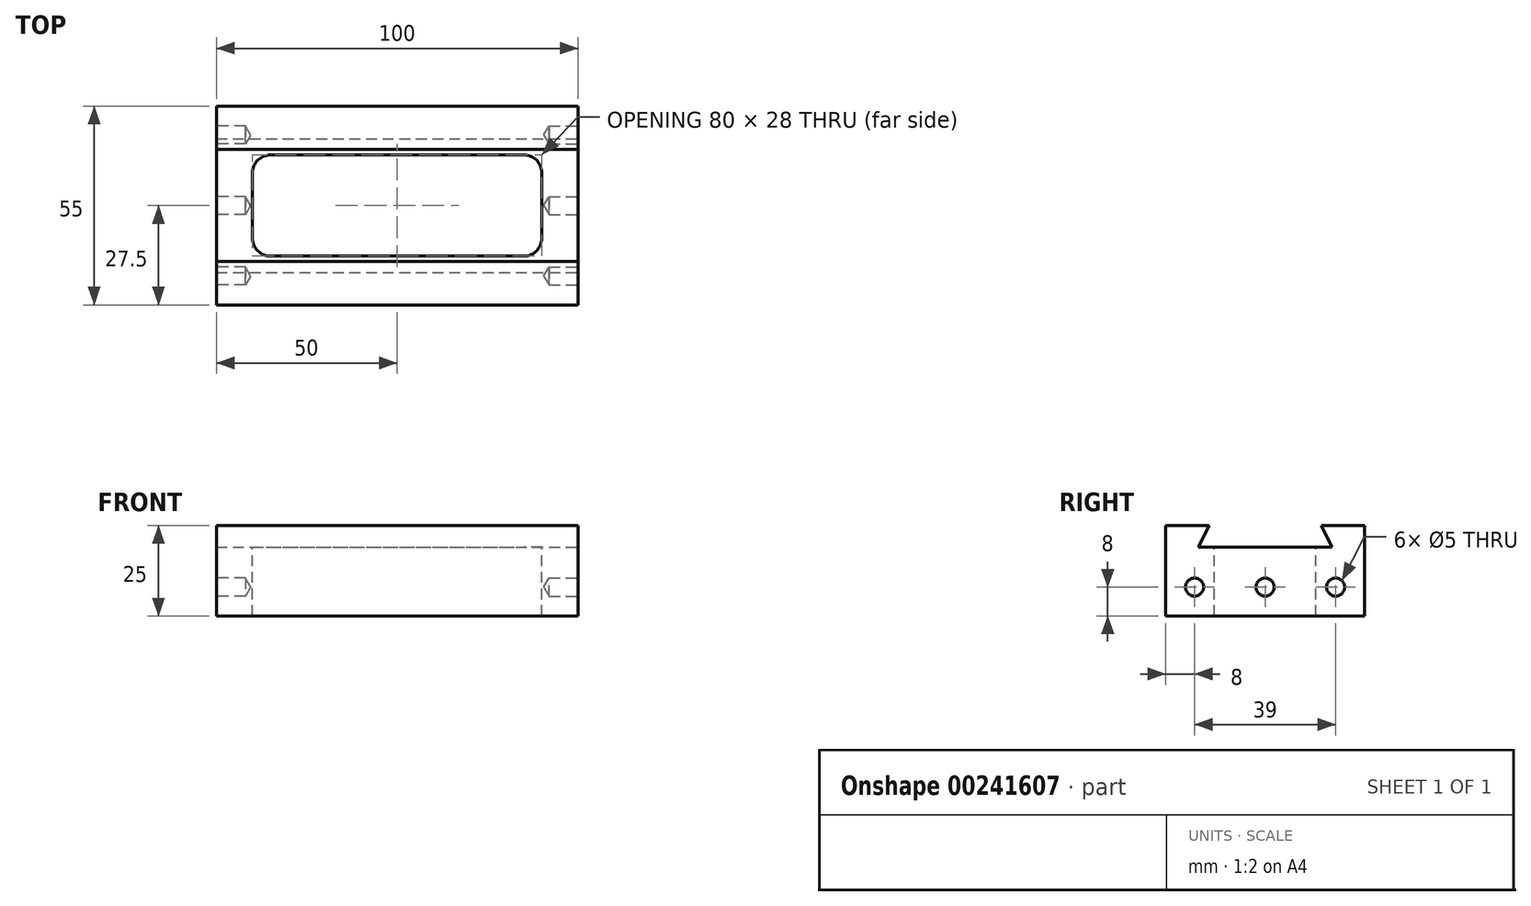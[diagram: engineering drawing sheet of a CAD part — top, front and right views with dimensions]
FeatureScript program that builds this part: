
annotation { "Feature Type Name" : "Feature", "Feature Type Description" : "" }
export const myFeature = defineFeature(function(context is Context, id is Id, definition is map)
    precondition{}
    {
        {
            var Q0;
            Q0=qCreatedBy(makeId("Top.planeOp"),FACE);
            var sketch = newSketch(context, id + "F0", { "sketchPlane" : qUnion([Q0])});
            skLineSegment(sketch, "E0.bottom", {"start": v(50, -27.5) * mm, "end": v(-50, -27.5) * mm});
            skLineSegment(sketch, "E0.top", {"start": v(50, 27.5) * mm, "end": v(-50, 27.5) * mm});
            skLineSegment(sketch, "E0.left", {"start": v(50, -27.5) * mm, "end": v(50, 27.5) * mm});
            skLineSegment(sketch, "E0.right", {"start": v(-50, -27.5) * mm, "end": v(-50, 27.5) * mm});
            skPoint(sketch, "E0.middle", {"position": v(0, 0) * mm});
            skSolve(sketch);
        }
        {
            var Q0;
            Q0 = qSketchRegion(id + "F0", true);
            extrude(context, id + "F1", {"entities" : qUnion([Q0]), "depth" : 25 * mm});
        }
        {
            var Q0;
            Q0=makeQuery(id+"F1.opExtrude","SWEPT_FACE",FACE,{"disambiguationData":[OSD([sQuery(id+"F0.wireOp",EDGE,"E0.left")])]});
            var sketch = newSketch(context, id + "F2", { "sketchPlane" : qUnion([Q0])});
            skLineSegment(sketch, "E1", {"start": v(-15.5, 25) * mm, "end": v(-18.5, 19) * mm});
            skLineSegment(sketch, "E2", {"start": v(-18.5, 19) * mm, "end": v(18.5, 19) * mm});
            skLineSegment(sketch, "E3", {"start": v(18.5, 19) * mm, "end": v(15.5, 25) * mm});
            skLineSegment(sketch, "E4", {"start": v(15.5, 25) * mm, "end": v(-15.5, 25) * mm});
            skSolve(sketch);
        }
        {
            var Q0;
            Q0 = qSketchRegion(id + "F2", true);
            var Q1;
            Q1=makeQuery(id+"F1.opExtrude","SWEPT_FACE",FACE,{"disambiguationData":[OSD([sQuery(id+"F0.wireOp",EDGE,"E0.right")])]});
            extrude(context, id + "F3", {"entities" : qUnion([Q0]), "operationType" : NewBodyOperationType.REMOVE, "endBound" : BoundingType.UP_TO_SURFACE, "oppositeDirection" : true, "endBoundEntityFace" : qUnion([Q1]), "depth" : 25 * mm});
        }
        {
            var Q0;
            Q0=makeQuery(id+"F3.boolean.opBoolean","COPY",FACE,{"derivedFrom":makeQuery(id+"F3.opExtrude","SWEPT_FACE",FACE,{"disambiguationData":[OSD([sQuery(id+"F2.wireOp",EDGE,"E2")])]})});
            var sketch = newSketch(context, id + "F4", { "sketchPlane" : qUnion([Q0])});
            skLineSegment(sketch, "E5.bottom", {"start": v(-35, 14) * mm, "end": v(35, 14) * mm});
            skLineSegment(sketch, "E5.top", {"start": v(-35, -14) * mm, "end": v(35, -14) * mm});
            skLineSegment(sketch, "E5.left", {"start": v(-40, 9) * mm, "end": v(-40, -9) * mm});
            skLineSegment(sketch, "E5.right", {"start": v(40, 9) * mm, "end": v(40, -9) * mm});
            skPoint(sketch, "E5.middle", {"position": v(0, 0) * mm});
            skPoint(sketch, "E6.visualSharp", {"position": v(-40, 14) * mm});
            skArc(sketch, "E6.filletArc", {"start": v(-35, 14) * mm, "mid": v(-38.54, 12.54) * mm, "end": v(-40, 9) * mm});
            skPoint(sketch, "E7.visualSharp", {"position": v(-40, -14) * mm});
            skArc(sketch, "E7.filletArc", {"start": v(-40, -9) * mm, "mid": v(-38.54, -12.54) * mm, "end": v(-35, -14) * mm});
            skPoint(sketch, "E8.visualSharp", {"position": v(40, 14) * mm});
            skArc(sketch, "E8.filletArc", {"start": v(40, 9) * mm, "mid": v(38.54, 12.54) * mm, "end": v(35, 14) * mm});
            skPoint(sketch, "E9.visualSharp", {"position": v(40, -14) * mm});
            skArc(sketch, "E9.filletArc", {"start": v(35, -14) * mm, "mid": v(38.54, -12.54) * mm, "end": v(40, -9) * mm});
            skSolve(sketch);
        }
        {
            var Q0;
            Q0 = qSketchRegion(id + "F4", true);
            var Q1;
            Q1=makeQuery(id+"F1.opExtrude","CAP_FACE",FACE,{"disambiguationData":[OSD([sQuery(id+"F0.wireOp",EDGE,"E0.bottom"),sQuery(id+"F0.wireOp",EDGE,"E0.top"),sQuery(id+"F0.wireOp",EDGE,"E0.left"),sQuery(id+"F0.wireOp",EDGE,"E0.right")])],"isStart":true});
            extrude(context, id + "F5", {"entities" : qUnion([Q0]), "operationType" : NewBodyOperationType.REMOVE, "endBound" : BoundingType.UP_TO_SURFACE, "oppositeDirection" : true, "endBoundEntityFace" : qUnion([Q1]), "depth" : 25 * mm});
        }
        {
            var Q0;
            Q0=makeQuery(id+"F1.opExtrude","SWEPT_FACE",FACE,{"disambiguationData":[OSD([sQuery(id+"F0.wireOp",EDGE,"E0.left")])]});
            var sketch = newSketch(context, id + "F6", { "sketchPlane" : qUnion([Q0])});
            skPoint(sketch, "E10", {"position": v(0, 8) * mm});
            skPoint(sketch, "E11", {"position": v(-19.5, 8) * mm});
            skPoint(sketch, "E12", {"position": v(19.5, 8) * mm});
            skSolve(sketch);
        }
        {
            var Q0;
            Q0=sQuery(id+"F6.wireOp",VERTEX,"E12");
            var Q1;
            Q1=sQuery(id+"F6.wireOp",VERTEX,"E10");
            var Q2;
            Q2=sQuery(id+"F6.wireOp",VERTEX,"E11");
            var Q3;
            Q3=makeQuery(id+"F1.opExtrude","SWEPT_BODY",BODY,{"disambiguationData":[OSD([sQuery(id+"F0.wireOp",EDGE,"E0.bottom"),sQuery(id+"F0.wireOp",EDGE,"E0.top"),sQuery(id+"F0.wireOp",EDGE,"E0.left"),sQuery(id+"F0.wireOp",EDGE,"E0.right")])]});
            hole(context, id + "F7", {"style" : HoleStyle.SIMPLE, "endStyle" : HoleEndStyle.BLIND, "holeDiameter" : 5 * mm, "holeDepth" : 8 * mm, "startFromSketch" : true, "locations" : qUnion([Q0, Q1, Q2]), "scope" : qUnion([Q3])});
        }
        {
            var Q0;
            Q0=makeQuery(id+"F1.opExtrude","SWEPT_FACE",FACE,{"disambiguationData":[OSD([sQuery(id+"F0.wireOp",EDGE,"E0.right")])]});
            var sketch = newSketch(context, id + "F8", { "sketchPlane" : qUnion([Q0])});
            skPoint(sketch, "E13", {"position": v(-19.5, 8) * mm});
            skPoint(sketch, "E14", {"position": v(0, 8) * mm});
            skPoint(sketch, "E15", {"position": v(19.5, 8) * mm});
            skSolve(sketch);
        }
        {
            var Q0;
            Q0=sQuery(id+"F8.wireOp",VERTEX,"E13");
            var Q1;
            Q1=sQuery(id+"F8.wireOp",VERTEX,"E14");
            var Q2;
            Q2=sQuery(id+"F8.wireOp",VERTEX,"E15");
            var Q3;
            Q3=makeQuery(id+"F1.opExtrude","SWEPT_BODY",BODY,{"disambiguationData":[OSD([sQuery(id+"F0.wireOp",EDGE,"E0.bottom"),sQuery(id+"F0.wireOp",EDGE,"E0.top"),sQuery(id+"F0.wireOp",EDGE,"E0.left"),sQuery(id+"F0.wireOp",EDGE,"E0.right")])]});
            hole(context, id + "F9", {"style" : HoleStyle.SIMPLE, "endStyle" : HoleEndStyle.BLIND, "holeDiameter" : 5 * mm, "holeDepth" : 8 * mm, "startFromSketch" : true, "locations" : qUnion([Q0, Q1, Q2]), "scope" : qUnion([Q3])});
        }
    });
